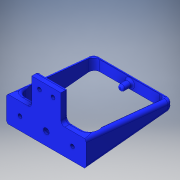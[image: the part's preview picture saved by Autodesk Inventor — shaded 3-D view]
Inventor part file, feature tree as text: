
AUTODESK INVENTOR PART (.ipt)
format: ipt  version: 2016 (Build 200138000, 138)  size: 362,496 bytes
history: native  units: in
note: dims shown in document units (in); Inventor stores cm internally (conversion verified against a paired STEP export)
features: sketch x11, other x3
ambient origin geometry x8: Origin, YZ Plane, XZ Plane, XY Plane, X Axis, Y Axis, Z Axis, Center Point
bodies: Solid1 (feature_tree)
feature tree (14):
  other  "Knee_hip_joint_right_side.ipt"
  other  "Solid1::Knee_hip_joint_right_side.ipt"
  other  "TaggingFeature1"
  sketch  "Sketch1"  dims[d0=0.3937in]
  sketch  "Sketch16"
  sketch  "Sketch17"
  sketch  "Sketch19"
  sketch  "Sketch20"
  sketch  "Sketch22"
  sketch  "Sketch24"
  sketch  "Sketch25"
  sketch  "Sketch30"
  sketch  "Sketch31"
  sketch  "Sketch32"
